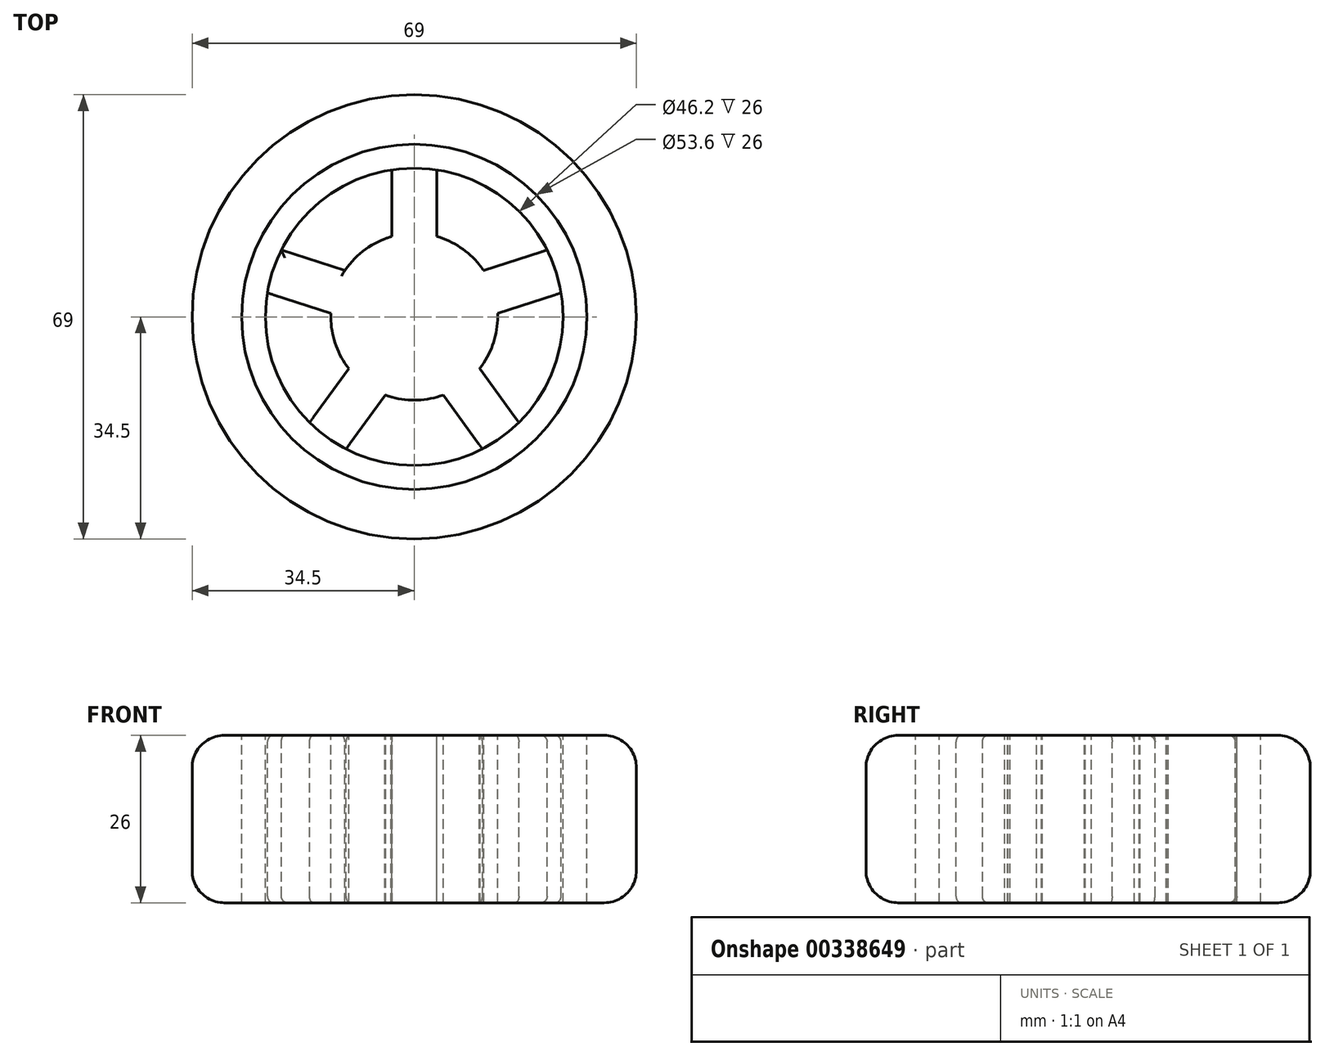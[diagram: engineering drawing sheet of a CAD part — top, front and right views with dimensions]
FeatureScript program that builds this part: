
annotation { "Feature Type Name" : "Feature", "Feature Type Description" : "" }
export const myFeature = defineFeature(function(context is Context, id is Id, definition is map)
    precondition{}
    {
        {
            var Q0;
            Q0=qCreatedBy(makeId("Top.planeOp"),FACE);
            var sketch = newSketch(context, id + "F0", { "sketchPlane" : qUnion([Q0])});
            skCircle(sketch, "E0", {"center": v(0, 0) * mm, "radius": 34.5 * mm});
            skCircle(sketch, "E1", {"center": v(0, 0) * mm, "radius": 26.8 * mm});
            skSolve(sketch);
        }
        {
            var Q0;
            Q0=makeQuery(id+"F0.imprint","IMPRINT",FACE,{"disambiguationData":[TD([[makeQuery(id+"F0.imprint","IMPRINT",EDGE,{"derivedFrom":sQuery(id+"F0.wireOp",EDGE,"E0")}),1.0]])]});
            extrude(context, id + "F1", {"entities" : qUnion([Q0]), "depth" : 26 * mm, "offsetDistance" : 25 * mm, "symmetric" : true});
        }
        {
            var Q0;
            Q0=makeQuery(id+"F1.opExtrude","CAP_FACE",FACE,{"disambiguationData":[OSD([sQuery(id+"F0.wireOp",EDGE,"E0"),sQuery(id+"F0.wireOp",EDGE,"E1")])],"isStart":false});
            var sketch = newSketch(context, id + "F2", { "sketchPlane" : qUnion([Q0])});
            skCircle(sketch, "E2", {"center": v(0, 0) * mm, "radius": 26.8 * mm});
            skCircle(sketch, "E3", {"center": v(0, 0) * mm, "radius": 23.1 * mm});
            skCircle(sketch, "E4", {"center": v(0, 0) * mm, "radius": 12.95 * mm});
            skLineSegment(sketch, "E5", {"start": v(-3.5, 12.47) * mm, "end": v(-3.5, 22.83) * mm});
            skLineSegment(sketch, "E6", {"start": v(3.5, 22.83) * mm, "end": v(3.5, 12.47) * mm});
            skArc(sketch, "E7", {"start": v(-4.56, 12.12) * mm, "mid": v(-3.8, 12.66) * mm, "end": v(-3.5, 13.55) * mm});
            skArc(sketch, "E8", {"start": v(3.5, 13.55) * mm, "mid": v(3.76, 12.72) * mm, "end": v(4.43, 12.17) * mm});
            skArc(sketch, "E9.1.0", {"start": v(-11.8, 7.52) * mm, "mid": v(-10.94, 7.5) * mm, "end": v(-10.2, 7.98) * mm});
            skLineSegment(sketch, "E9.1.1", {"start": v(-20.63, 10.38) * mm, "end": v(-10.78, 7.18) * mm});
            skLineSegment(sketch, "E9.1.2", {"start": v(-12.94, 0.52) * mm, "end": v(-22.8, 3.73) * mm});
            skArc(sketch, "E9.1.3", {"start": v(-12.94, -0.59) * mm, "mid": v(-13.22, 0.3) * mm, "end": v(-13.97, 0.86) * mm});
            skArc(sketch, "E9.2.0", {"start": v(-10.8, -8.9) * mm, "mid": v(-10.51, -8.08) * mm, "end": v(-10.74, -7.24) * mm});
            skLineSegment(sketch, "E9.2.1", {"start": v(-16.25, -16.42) * mm, "end": v(-10.16, -8.03) * mm});
            skLineSegment(sketch, "E9.2.2", {"start": v(-4.5, -12.14) * mm, "end": v(-10.59, -20.53) * mm});
            skArc(sketch, "E9.2.3", {"start": v(-3.44, -12.48) * mm, "mid": v(-4.38, -12.48) * mm, "end": v(-5.14, -13.02) * mm});
            skArc(sketch, "E9.3.0", {"start": v(5.14, -13.02) * mm, "mid": v(4.44, -12.5) * mm, "end": v(3.57, -12.45) * mm});
            skLineSegment(sketch, "E9.3.1", {"start": v(10.59, -20.53) * mm, "end": v(4.5, -12.14) * mm});
            skLineSegment(sketch, "E9.3.2", {"start": v(10.16, -8.03) * mm, "end": v(16.25, -16.42) * mm});
            skArc(sketch, "E9.3.3", {"start": v(10.81, -7.13) * mm, "mid": v(10.51, -8.02) * mm, "end": v(10.8, -8.9) * mm});
            skArc(sketch, "E9.4.0", {"start": v(13.97, 0.86) * mm, "mid": v(13.26, 0.36) * mm, "end": v(12.94, -0.46) * mm});
            skLineSegment(sketch, "E9.4.1", {"start": v(22.8, 3.73) * mm, "end": v(12.94, 0.52) * mm});
            skLineSegment(sketch, "E9.4.2", {"start": v(10.78, 7.18) * mm, "end": v(20.63, 10.38) * mm});
            skArc(sketch, "E9.4.3", {"start": v(10.12, 8.08) * mm, "mid": v(10.87, 7.52) * mm, "end": v(11.8, 7.52) * mm});
            skSolve(sketch);
        }
        {
            var Q0;
            {var subQ0=sQuery(id+"F2.wireOp",EDGE,"E5");var subQ1=sQuery(id+"F2.wireOp",EDGE,"E3");var subQ2=makeQuery(id+"F2.imprint","INTERSECT",VERTEX,{"derivedFrom":[subQ1,subQ0]});Q0=makeQuery(id+"F2.imprint","IMPRINT",FACE,{"disambiguationData":[TD([[makeQuery(id+"F2.imprint","IMPRINT",EDGE,{"disambiguationData":[TD([[subQ2,1.0]])],"derivedFrom":subQ1}),1.0]])]});}
            var Q1;
            {var subQ0=sQuery(id+"F2.wireOp",EDGE,"E4");var subQ21=makeQuery(id+"F2.imprint","INTERSECT",VERTEX,{"derivedFrom":[subQ0,sQuery(id+"F2.wireOp",EDGE,"E9.4.1")]});Q1=makeQuery(id+"F2.imprint","IMPRINT",FACE,{"disambiguationData":[TD([[makeQuery(id+"F2.imprint","IMPRINT",EDGE,{"disambiguationData":[TD([[subQ21,-1.0]])],"derivedFrom":subQ0}),1.0]])]});}
            var Q2;
            {var subQ0=sQuery(id+"F2.wireOp",EDGE,"E9.1.1");var subQ2=sQuery(id+"F2.wireOp",EDGE,"E3");var subQ3=makeQuery(id+"F2.imprint","INTERSECT",VERTEX,{"derivedFrom":[subQ2,subQ0]});Q2=makeQuery(id+"F2.imprint","IMPRINT",FACE,{"disambiguationData":[TD([[makeQuery(id+"F2.imprint","IMPRINT",EDGE,{"disambiguationData":[TD([[subQ3,-1.0]])],"derivedFrom":subQ2}),1.0]])]});}
            var Q3;
            {var subQ0=sQuery(id+"F2.wireOp",EDGE,"E9.2.1");var subQ2=sQuery(id+"F2.wireOp",EDGE,"E3");var subQ3=makeQuery(id+"F2.imprint","INTERSECT",VERTEX,{"derivedFrom":[subQ2,subQ0]});Q3=makeQuery(id+"F2.imprint","IMPRINT",FACE,{"disambiguationData":[TD([[makeQuery(id+"F2.imprint","IMPRINT",EDGE,{"disambiguationData":[TD([[subQ3,-1.0]])],"derivedFrom":subQ2}),1.0]])]});}
            var Q4;
            {var subQ0=sQuery(id+"F2.wireOp",EDGE,"E9.3.1");var subQ2=sQuery(id+"F2.wireOp",EDGE,"E3");var subQ3=makeQuery(id+"F2.imprint","INTERSECT",VERTEX,{"derivedFrom":[subQ2,subQ0]});Q4=makeQuery(id+"F2.imprint","IMPRINT",FACE,{"disambiguationData":[TD([[makeQuery(id+"F2.imprint","IMPRINT",EDGE,{"disambiguationData":[TD([[subQ3,-1.0]])],"derivedFrom":subQ2}),1.0]])]});}
            var Q5;
            {var subQ0=sQuery(id+"F2.wireOp",EDGE,"E9.4.1");var subQ2=sQuery(id+"F2.wireOp",EDGE,"E3");var subQ3=makeQuery(id+"F2.imprint","INTERSECT",VERTEX,{"derivedFrom":[subQ2,subQ0]});Q5=makeQuery(id+"F2.imprint","IMPRINT",FACE,{"disambiguationData":[TD([[makeQuery(id+"F2.imprint","IMPRINT",EDGE,{"disambiguationData":[TD([[subQ3,-1.0]])],"derivedFrom":subQ2}),1.0]])]});}
            extrude(context, id + "F3", {"entities" : qUnion([Q0, Q1, Q2, Q3, Q4, Q5]), "oppositeDirection" : true, "depth" : 26 * mm, "offsetDistance" : 25 * mm});
        }
        {
            var Q0;
            Q0=makeQuery(id+"F2.imprint","IMPRINT",FACE,{"disambiguationData":[TD([[makeQuery(id+"F2.imprint","IMPRINT",EDGE,{"derivedFrom":sQuery(id+"F2.wireOp",EDGE,"E2")}),1.0]])]});
            extrude(context, id + "F4", {"entities" : qUnion([Q0]), "oppositeDirection" : true, "depth" : 26 * mm, "offsetDistance" : 25 * mm});
        }
        {
            var Q0;
            Q0=makeQuery(id+"F1.opExtrude","CAP_EDGE",EDGE,{"disambiguationData":[OSD([sQuery(id+"F0.wireOp",EDGE,"E0")])],"isStart":true});
            var Q1;
            Q1=makeQuery(id+"F1.opExtrude","CAP_EDGE",EDGE,{"disambiguationData":[OSD([sQuery(id+"F0.wireOp",EDGE,"E0")])],"isStart":false});
            fillet(context, id + "F5", {"entities" : qUnion([Q0, Q1]), "radius" : 5 * mm, "tangentPropagation" : true, "allowEdgeOverflow" : false});
        }
        {
            var Q0;
            {var subQ0=sQuery(id+"F2.wireOp",EDGE,"E3");Q0=makeQuery(id+"F3.opExtrude","CAP_EDGE",EDGE,{"disambiguationData":[OSD([subQ0]),TDD([makeQuery(id+"F2.imprint","IMPRINT",EDGE,{"disambiguationData":[TD([[makeQuery(id+"F2.imprint","INTERSECT",VERTEX,{"derivedFrom":[subQ0,sQuery(id+"F2.wireOp",EDGE,"E9.2.1")]}),-1.0]])],"derivedFrom":subQ0})])],"isStart":false});}
            var Q1;
            {var subQ0=sQuery(id+"F2.wireOp",EDGE,"E3");Q1=makeQuery(id+"F3.opExtrude","CAP_EDGE",EDGE,{"disambiguationData":[OSD([subQ0]),TDD([makeQuery(id+"F2.imprint","IMPRINT",EDGE,{"disambiguationData":[TD([[makeQuery(id+"F2.imprint","INTERSECT",VERTEX,{"derivedFrom":[subQ0,sQuery(id+"F2.wireOp",EDGE,"E9.3.1")]}),-1.0]])],"derivedFrom":subQ0})])],"isStart":false});}
            var Q2;
            {var subQ0=sQuery(id+"F2.wireOp",EDGE,"E3");Q2=makeQuery(id+"F3.opExtrude","CAP_EDGE",EDGE,{"disambiguationData":[OSD([subQ0]),TDD([makeQuery(id+"F2.imprint","IMPRINT",EDGE,{"disambiguationData":[TD([[makeQuery(id+"F2.imprint","INTERSECT",VERTEX,{"derivedFrom":[subQ0,sQuery(id+"F2.wireOp",EDGE,"E9.4.1")]}),-1.0]])],"derivedFrom":subQ0})])],"isStart":false});}
            var Q3;
            {var subQ0=sQuery(id+"F2.wireOp",EDGE,"E3");Q3=makeQuery(id+"F3.opExtrude","CAP_EDGE",EDGE,{"disambiguationData":[OSD([subQ0]),TDD([makeQuery(id+"F2.imprint","IMPRINT",EDGE,{"disambiguationData":[TD([[makeQuery(id+"F2.imprint","INTERSECT",VERTEX,{"derivedFrom":[subQ0,sQuery(id+"F2.wireOp",EDGE,"E5")]}),1.0]])],"derivedFrom":subQ0})])],"isStart":false});}
            var Q4;
            {var subQ0=sQuery(id+"F2.wireOp",EDGE,"E3");Q4=makeQuery(id+"F3.opExtrude","CAP_EDGE",EDGE,{"disambiguationData":[OSD([subQ0]),TDD([makeQuery(id+"F2.imprint","IMPRINT",EDGE,{"disambiguationData":[TD([[makeQuery(id+"F2.imprint","INTERSECT",VERTEX,{"derivedFrom":[subQ0,sQuery(id+"F2.wireOp",EDGE,"E9.1.1")]}),-1.0]])],"derivedFrom":subQ0})])],"isStart":false});}
            var Q5;
            {var subQ0=sQuery(id+"F2.wireOp",EDGE,"E3");Q5=makeQuery(id+"F3.opExtrude","CAP_EDGE",EDGE,{"disambiguationData":[OSD([subQ0]),TDD([makeQuery(id+"F2.imprint","IMPRINT",EDGE,{"disambiguationData":[TD([[makeQuery(id+"F2.imprint","INTERSECT",VERTEX,{"derivedFrom":[subQ0,sQuery(id+"F2.wireOp",EDGE,"E9.1.1")]}),-1.0]])],"derivedFrom":subQ0})])],"isStart":true});}
            var Q6;
            {var subQ0=sQuery(id+"F2.wireOp",EDGE,"E3");Q6=makeQuery(id+"F3.opExtrude","CAP_EDGE",EDGE,{"disambiguationData":[OSD([subQ0]),TDD([makeQuery(id+"F2.imprint","IMPRINT",EDGE,{"disambiguationData":[TD([[makeQuery(id+"F2.imprint","INTERSECT",VERTEX,{"derivedFrom":[subQ0,sQuery(id+"F2.wireOp",EDGE,"E5")]}),1.0]])],"derivedFrom":subQ0})])],"isStart":true});}
            var Q7;
            {var subQ0=sQuery(id+"F2.wireOp",EDGE,"E3");Q7=makeQuery(id+"F3.opExtrude","CAP_EDGE",EDGE,{"disambiguationData":[OSD([subQ0]),TDD([makeQuery(id+"F2.imprint","IMPRINT",EDGE,{"disambiguationData":[TD([[makeQuery(id+"F2.imprint","INTERSECT",VERTEX,{"derivedFrom":[subQ0,sQuery(id+"F2.wireOp",EDGE,"E9.2.1")]}),-1.0]])],"derivedFrom":subQ0})])],"isStart":true});}
            var Q8;
            {var subQ0=sQuery(id+"F2.wireOp",EDGE,"E3");Q8=makeQuery(id+"F3.opExtrude","CAP_EDGE",EDGE,{"disambiguationData":[OSD([subQ0]),TDD([makeQuery(id+"F2.imprint","IMPRINT",EDGE,{"disambiguationData":[TD([[makeQuery(id+"F2.imprint","INTERSECT",VERTEX,{"derivedFrom":[subQ0,sQuery(id+"F2.wireOp",EDGE,"E9.3.1")]}),-1.0]])],"derivedFrom":subQ0})])],"isStart":true});}
            var Q9;
            {var subQ0=sQuery(id+"F2.wireOp",EDGE,"E3");Q9=makeQuery(id+"F3.opExtrude","CAP_EDGE",EDGE,{"disambiguationData":[OSD([subQ0]),TDD([makeQuery(id+"F2.imprint","IMPRINT",EDGE,{"disambiguationData":[TD([[makeQuery(id+"F2.imprint","INTERSECT",VERTEX,{"derivedFrom":[subQ0,sQuery(id+"F2.wireOp",EDGE,"E9.4.1")]}),-1.0]])],"derivedFrom":subQ0})])],"isStart":true});}
            var Q10;
            {var subQ0=sQuery(id+"F0.wireOp",EDGE,"E0");Q10=makeQuery(id+"F5.opFillet","BLEND_EDGE",EDGE,{"blendedFrom":[makeQuery(id+"F1.opExtrude","CAP_EDGE",EDGE,{"disambiguationData":[OSD([subQ0])],"isStart":true}),makeQuery(id+"F1.opExtrude","SWEPT_FACE",FACE,{"disambiguationData":[OSD([subQ0])]})],"blendedInto":[makeQuery(id+"F1.opExtrude","SWEPT_FACE",FACE,{"disambiguationData":[OSD([subQ0])]})]});}
            var Q11;
            Q11=makeQuery(id+"F3.opExtrude","CAP_EDGE",EDGE,{"disambiguationData":[OSD([sQuery(id+"F2.wireOp",EDGE,"E9.1.1")])],"isStart":true});
            fillet(context, id + "F6", {"entities" : qUnion([Q0, Q1, Q2, Q3, Q4, Q5, Q6, Q7, Q8, Q9, Q10, Q11]), "radius" : 1 * mm, "tangentPropagation" : true, "allowEdgeOverflow" : false});
        }
    });
